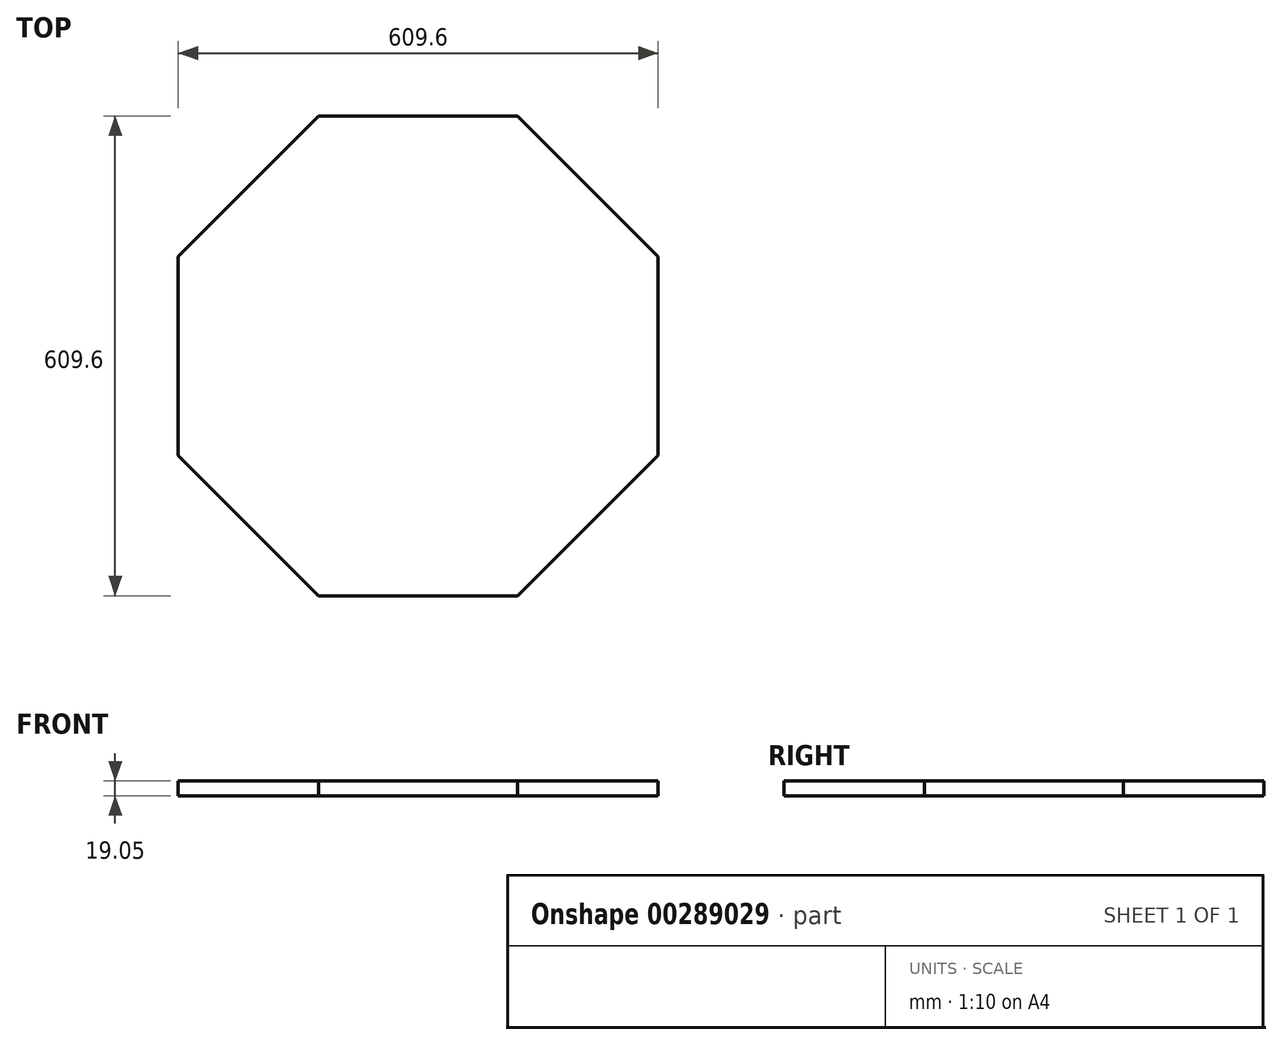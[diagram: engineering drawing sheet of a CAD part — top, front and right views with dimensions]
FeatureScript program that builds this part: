
annotation { "Feature Type Name" : "Feature", "Feature Type Description" : "" }
export const myFeature = defineFeature(function(context is Context, id is Id, definition is map)
    precondition{}
    {
        {
            var Q0;
            Q0=qCreatedBy(makeId("Top.planeOp"),FACE);
            var sketch = newSketch(context, id + "F0", { "sketchPlane" : qUnion([Q0])});
            skCircle(sketch, "E0.cCircle", {"center": v(0, 0) * mm, "radius": 304.8 * mm, "construction": true});
            skLineSegment(sketch, "E0.0", {"start": v(126.25, -304.8) * mm, "end": v(-126.25, -304.8) * mm});
            skLineSegment(sketch, "E0.1", {"start": v(-126.25, -304.8) * mm, "end": v(-304.8, -126.25) * mm});
            skLineSegment(sketch, "E0.2", {"start": v(-304.8, -126.25) * mm, "end": v(-304.8, 126.25) * mm});
            skLineSegment(sketch, "E0.3", {"start": v(-304.8, 126.25) * mm, "end": v(-126.25, 304.8) * mm});
            skLineSegment(sketch, "E0.4", {"start": v(-126.25, 304.8) * mm, "end": v(126.25, 304.8) * mm});
            skLineSegment(sketch, "E0.5", {"start": v(126.25, 304.8) * mm, "end": v(304.8, 126.25) * mm});
            skLineSegment(sketch, "E0.6", {"start": v(304.8, 126.25) * mm, "end": v(304.8, -126.25) * mm});
            skLineSegment(sketch, "E0.7", {"start": v(304.8, -126.25) * mm, "end": v(126.25, -304.8) * mm});
            skPoint(sketch, "E0.0.midPoint", {"position": v(0, -304.8) * mm});
            skSolve(sketch);
        }
        {
            var Q0;
            Q0 = qSketchRegion(id + "F0", true);
            extrude(context, id + "F1", {"entities" : qUnion([Q0]), "depth" : 19.05 * mm});
        }
    });
